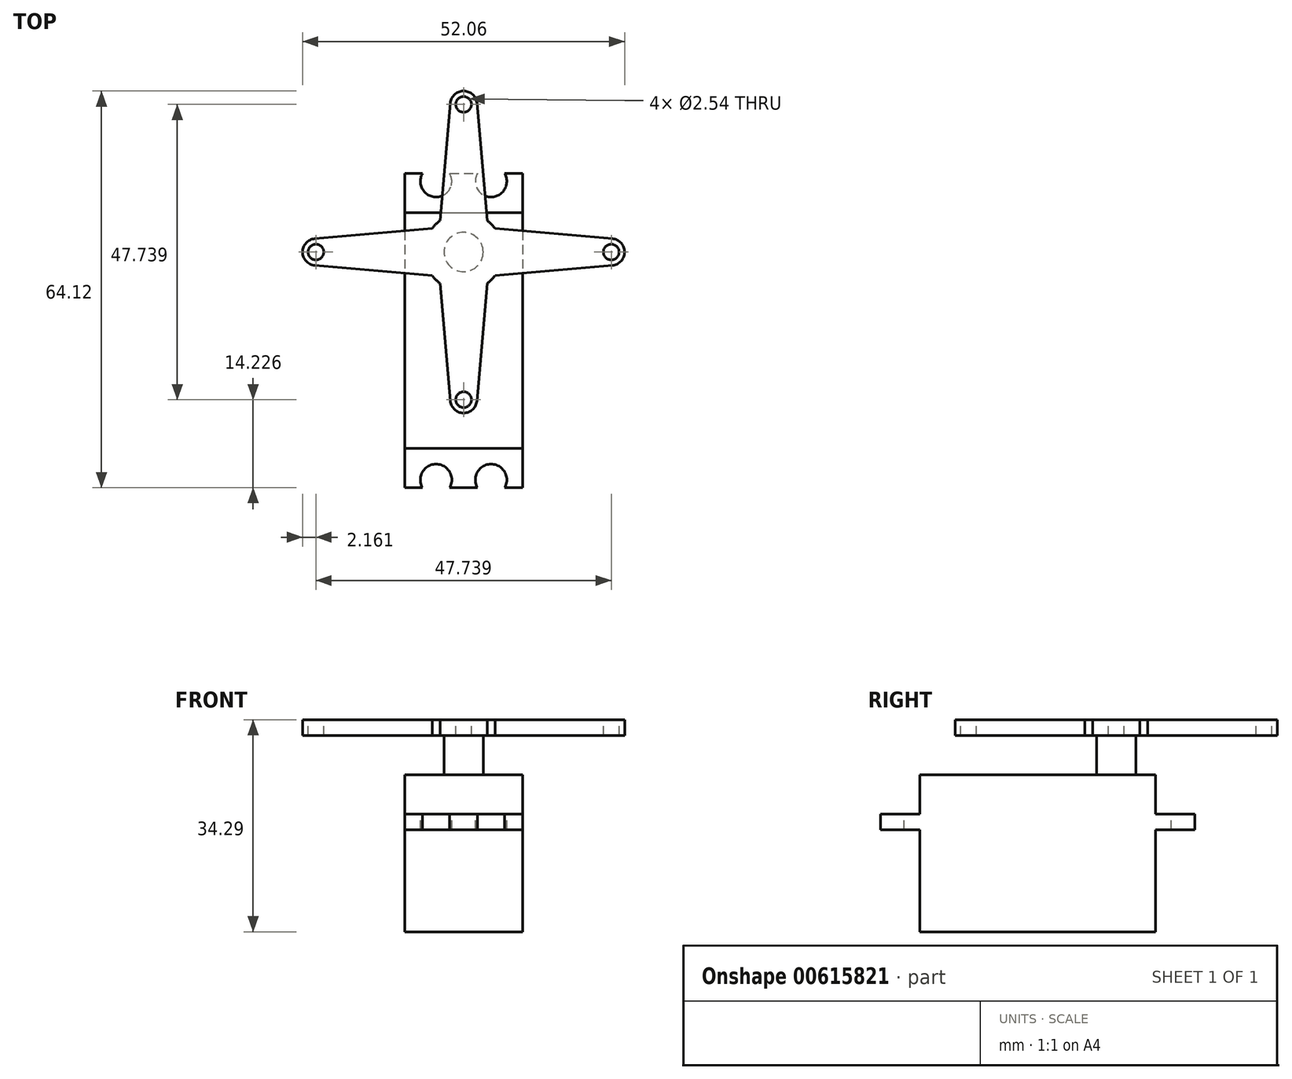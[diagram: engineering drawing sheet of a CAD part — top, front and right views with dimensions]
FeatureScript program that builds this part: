
annotation { "Feature Type Name" : "Feature", "Feature Type Description" : "" }
export const myFeature = defineFeature(function(context is Context, id is Id, definition is map)
    precondition{}
    {
        {
            var Q0;
            Q0=qCreatedBy(makeId("Top.planeOp"),FACE);
            var sketch = newSketch(context, id + "F0", { "sketchPlane" : qUnion([Q0])});
            skLineSegment(sketch, "E0.bottom", {"start": v(-45.11, 33.45) * mm, "end": v(-26.06, 33.45) * mm});
            skLineSegment(sketch, "E0.top", {"start": v(-45.11, -4.65) * mm, "end": v(-26.06, -4.65) * mm});
            skLineSegment(sketch, "E0.left", {"start": v(-45.11, 33.45) * mm, "end": v(-45.11, -4.65) * mm});
            skLineSegment(sketch, "E0.right", {"start": v(-26.06, 33.45) * mm, "end": v(-26.06, -4.65) * mm});
            skSolve(sketch);
        }
        {
            var Q0;
            Q0 = qSketchRegion(id + "F0", true);
            extrude(context, id + "F1", {"entities" : qUnion([Q0]), "depth" : 16.5 * mm, "offsetDistance" : 25.4 * mm});
        }
        {
            var Q0;
            Q0=makeQuery(id+"F1.opExtrude","CAP_FACE",FACE,{"disambiguationData":[OSD([sQuery(id+"F0.wireOp",EDGE,"E0.bottom"),sQuery(id+"F0.wireOp",EDGE,"E0.top"),sQuery(id+"F0.wireOp",EDGE,"E0.left"),sQuery(id+"F0.wireOp",EDGE,"E0.right")])],"isStart":false});
            var sketch = newSketch(context, id + "F2", { "sketchPlane" : qUnion([Q0])});
            skLineSegment(sketch, "E1.bottom", {"start": v(-45.11, 39.8) * mm, "end": v(-26.06, 39.8) * mm});
            skLineSegment(sketch, "E1.top", {"start": v(-45.11, -11) * mm, "end": v(-26.06, -11) * mm});
            skLineSegment(sketch, "E1.left", {"start": v(-45.11, 39.8) * mm, "end": v(-45.11, -11) * mm});
            skLineSegment(sketch, "E1.right", {"start": v(-26.06, 39.8) * mm, "end": v(-26.06, -11) * mm});
            skSolve(sketch);
        }
        {
            var Q0;
            Q0 = qSketchRegion(id + "F2", true);
            extrude(context, id + "F3", {"entities" : qUnion([Q0]), "operationType" : NewBodyOperationType.ADD, "depth" : 2.54 * mm, "offsetDistance" : 25.4 * mm});
        }
        {
            var Q0;
            Q0=makeQuery(id+"F3.opExtrude","CAP_FACE",FACE,{"disambiguationData":[OSD([sQuery(id+"F2.wireOp",EDGE,"E1.bottom"),sQuery(id+"F2.wireOp",EDGE,"E1.top"),sQuery(id+"F2.wireOp",EDGE,"E1.left"),sQuery(id+"F2.wireOp",EDGE,"E1.right")])],"isStart":false});
            var sketch = newSketch(context, id + "F4", { "sketchPlane" : qUnion([Q0])});
            skCircle(sketch, "E2", {"center": v(-40.03, 38.53) * mm, "radius": 2.54 * mm});
            skCircle(sketch, "E3", {"center": v(-31.14, 38.53) * mm, "radius": 2.54 * mm});
            skCircle(sketch, "E4", {"center": v(-31.14, -9.73) * mm, "radius": 2.54 * mm});
            skCircle(sketch, "E5", {"center": v(-40.03, -9.73) * mm, "radius": 2.54 * mm});
            skSolve(sketch);
        }
        {
            var Q0;
            Q0 = qSketchRegion(id + "F4", true);
            extrude(context, id + "F5", {"entities" : qUnion([Q0]), "operationType" : NewBodyOperationType.REMOVE, "oppositeDirection" : true, "depth" : 2.54 * mm, "offsetDistance" : 25.4 * mm});
        }
        {
            var Q0;
            Q0=makeQuery(id+"F3.opExtrude","CAP_FACE",FACE,{"disambiguationData":[OSD([sQuery(id+"F2.wireOp",EDGE,"E1.bottom"),sQuery(id+"F2.wireOp",EDGE,"E1.top"),sQuery(id+"F2.wireOp",EDGE,"E1.left"),sQuery(id+"F2.wireOp",EDGE,"E1.right")])],"isStart":false});
            var sketch = newSketch(context, id + "F6", { "sketchPlane" : qUnion([Q0])});
            skLineSegment(sketch, "E6.bottom", {"start": v(-45.11, 33.45) * mm, "end": v(-26.06, 33.45) * mm});
            skLineSegment(sketch, "E6.top", {"start": v(-45.11, -4.65) * mm, "end": v(-26.06, -4.65) * mm});
            skLineSegment(sketch, "E6.left", {"start": v(-45.11, 33.45) * mm, "end": v(-45.11, -4.65) * mm});
            skLineSegment(sketch, "E6.right", {"start": v(-26.06, 33.45) * mm, "end": v(-26.06, -4.65) * mm});
            skSolve(sketch);
        }
        {
            var Q0;
            Q0 = qSketchRegion(id + "F6", true);
            extrude(context, id + "F7", {"entities" : qUnion([Q0]), "operationType" : NewBodyOperationType.ADD, "depth" : 6.35 * mm, "offsetDistance" : 25.4 * mm});
        }
        {
            var Q0;
            Q0=makeQuery(id+"F7.opExtrude","CAP_FACE",FACE,{"disambiguationData":[OSD([sQuery(id+"F6.wireOp",EDGE,"E6.bottom"),sQuery(id+"F6.wireOp",EDGE,"E6.top"),sQuery(id+"F6.wireOp",EDGE,"E6.left"),sQuery(id+"F6.wireOp",EDGE,"E6.right")])],"isStart":false});
            var sketch = newSketch(context, id + "F8", { "sketchPlane" : qUnion([Q0])});
            skCircle(sketch, "E7", {"center": v(-35.59, 27.1) * mm, "radius": 3.18 * mm});
            skSolve(sketch);
        }
        {
            var Q0;
            Q0 = qSketchRegion(id + "F8", true);
            extrude(context, id + "F9", {"entities" : qUnion([Q0]), "operationType" : NewBodyOperationType.ADD, "depth" : 6.35 * mm, "offsetDistance" : 25.4 * mm});
        }
        {
            var Q0;
            Q0=makeQuery(id+"F9.opExtrude","CAP_FACE",FACE,{"disambiguationData":[OSD([sQuery(id+"F8.wireOp",EDGE,"E7")])],"isStart":false});
            var sketch = newSketch(context, id + "F10", { "sketchPlane" : qUnion([Q0])});
            skCircle(sketch, "E8", {"center": v(-35.59, 27.1) * mm, "radius": 6.35 * mm});
            skSolve(sketch);
        }
        {
            var Q0;
            Q0 = qSketchRegion(id + "F10", true);
            extrude(context, id + "F11", {"entities" : qUnion([Q0]), "operationType" : NewBodyOperationType.ADD, "depth" : 2.54 * mm, "offsetDistance" : 25.4 * mm});
        }
        {
            var Q0;
            Q0=makeQuery(id+"F11.opExtrude","CAP_FACE",FACE,{"disambiguationData":[OSD([sQuery(id+"F10.wireOp",EDGE,"E8")])],"isStart":false});
            var sketch = newSketch(context, id + "F12", { "sketchPlane" : qUnion([Q0])});
            skLineSegment(sketch, "E9", {"start": v(-39.4, 32.18) * mm, "end": v(-37.74, 51.15) * mm});
            skLineSegment(sketch, "E10", {"start": v(-31.78, 32.18) * mm, "end": v(-33.44, 51.15) * mm});
            skArc(sketch, "E11", {"start": v(-33.44, 51.15) * mm, "mid": v(-35.59, 53.12) * mm, "end": v(-37.74, 51.15) * mm});
            skCircle(sketch, "E12", {"center": v(-35.59, 50.96) * mm, "radius": 1.27 * mm});
            skArc(sketch, "E13", {"start": v(-31.78, 32.18) * mm, "mid": v(-35.59, 33.45) * mm, "end": v(-39.4, 32.18) * mm});
            skLineSegment(sketch, "E14", {"start": v(-35.59, 12.49) * mm, "end": v(-35.59, 61.43) * mm, "construction": true});
            skPoint(sketch, "E14.endSnap0", {"position": v(-35.59, 53.12) * mm});
            skLineSegment(sketch, "E15", {"start": v(-48.76, 27.1) * mm, "end": v(-15.72, 27.1) * mm, "construction": true});
            skLineSegment(sketch, "E16", {"start": v(-30.5, 30.9) * mm, "end": v(-11.53, 29.25) * mm});
            skLineSegment(sketch, "E17", {"start": v(-30.5, 23.29) * mm, "end": v(-11.53, 24.95) * mm});
            skArc(sketch, "E18", {"start": v(-11.53, 24.95) * mm, "mid": v(-9.56, 27.1) * mm, "end": v(-11.53, 29.25) * mm});
            skCircle(sketch, "E19", {"center": v(-11.72, 27.1) * mm, "radius": 1.27 * mm});
            skLineSegment(sketch, "E20", {"start": v(-31.78, 22.02) * mm, "end": v(-33.44, 3.04) * mm});
            skLineSegment(sketch, "E21", {"start": v(-39.4, 22.02) * mm, "end": v(-37.74, 3.04) * mm});
            skArc(sketch, "E22", {"start": v(-30.5, 23.29) * mm, "mid": v(-29.24, 27.1) * mm, "end": v(-30.5, 30.9) * mm});
            skArc(sketch, "E23", {"start": v(-37.74, 3.04) * mm, "mid": v(-35.59, 1.07) * mm, "end": v(-33.44, 3.04) * mm});
            skArc(sketch, "E24", {"start": v(-39.4, 22.02) * mm, "mid": v(-35.59, 20.75) * mm, "end": v(-31.78, 22.02) * mm});
            skLineSegment(sketch, "E25", {"start": v(-40.67, 30.9) * mm, "end": v(-59.65, 29.25) * mm});
            skLineSegment(sketch, "E26", {"start": v(-40.67, 23.29) * mm, "end": v(-59.65, 24.95) * mm});
            skArc(sketch, "E27", {"start": v(-59.65, 29.25) * mm, "mid": v(-61.62, 27.1) * mm, "end": v(-59.65, 24.95) * mm});
            skArc(sketch, "E28", {"start": v(-40.67, 30.9) * mm, "mid": v(-41.94, 27.1) * mm, "end": v(-40.67, 23.29) * mm});
            skCircle(sketch, "E29", {"center": v(-59.46, 27.1) * mm, "radius": 1.27 * mm});
            skCircle(sketch, "E30", {"center": v(-35.59, 3.23) * mm, "radius": 1.27 * mm});
            skSolve(sketch);
        }
        {
            var Q0;
            Q0 = qSketchRegion(id + "F12", true);
            extrude(context, id + "F13", {"entities" : qUnion([Q0]), "operationType" : NewBodyOperationType.ADD, "oppositeDirection" : true, "depth" : 2.54 * mm, "offsetDistance" : 25.4 * mm});
        }
    });
